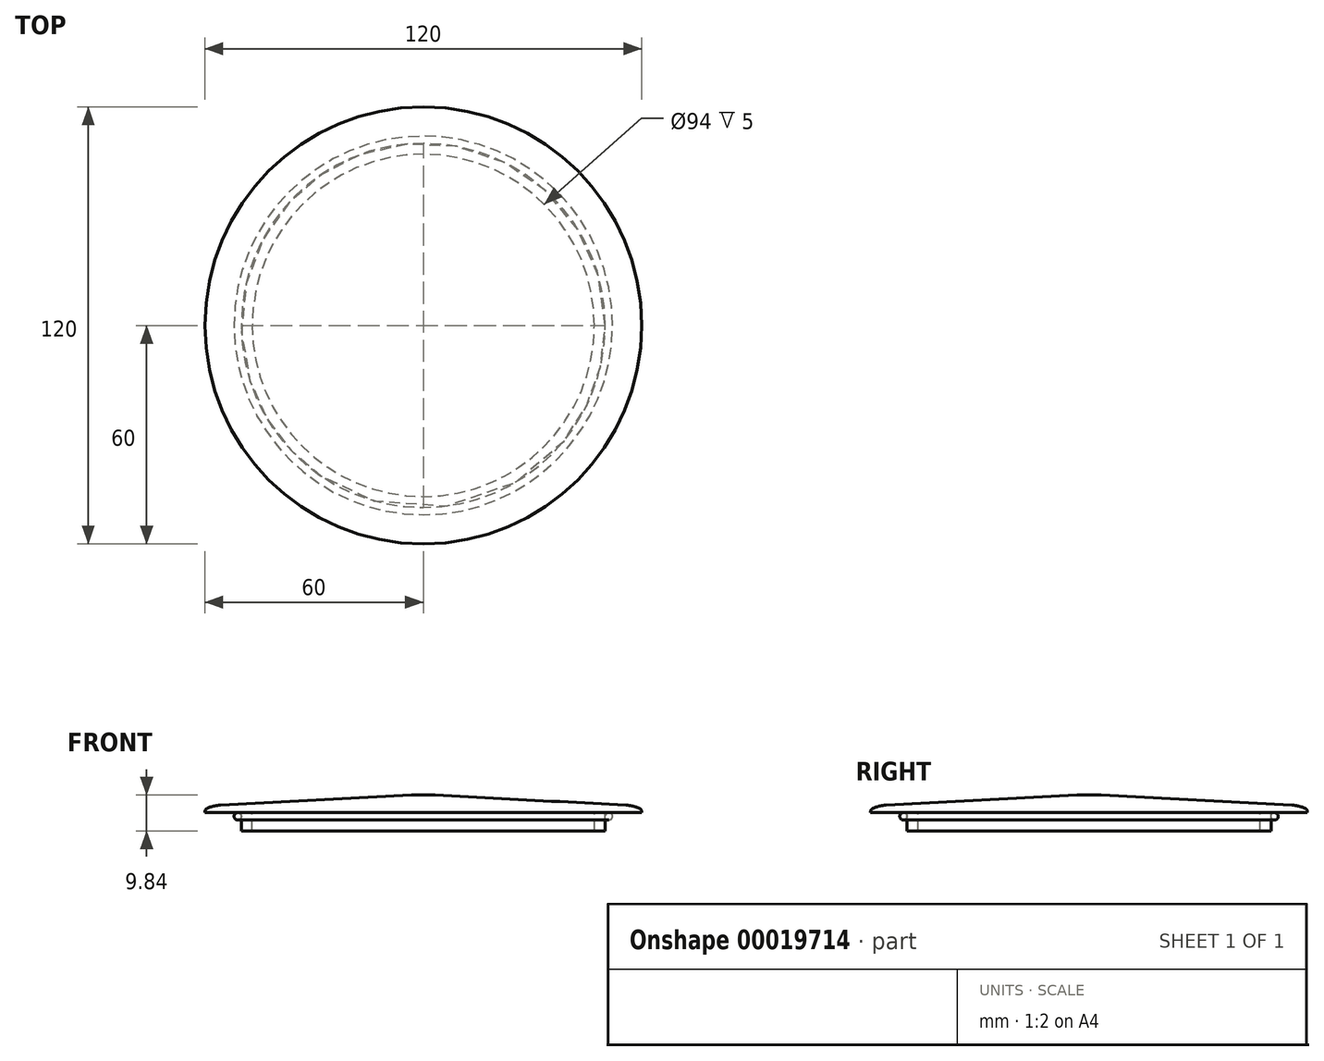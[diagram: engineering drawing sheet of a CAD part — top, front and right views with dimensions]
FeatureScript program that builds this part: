
annotation { "Feature Type Name" : "Feature", "Feature Type Description" : "" }
export const myFeature = defineFeature(function(context is Context, id is Id, definition is map)
    precondition{}
    {
        {
            var Q0;
            Q0=qCreatedBy(makeId("Front.planeOp"),FACE);
            var sketch = newSketch(context, id + "F0", { "sketchPlane" : qUnion([Q0])});
            skLineSegment(sketch, "E0", {"start": v(50, 0) * mm, "end": v(50, 5) * mm});
            skLineSegment(sketch, "E1", {"start": v(50, 5) * mm, "end": v(60, 5) * mm});
            skLineSegment(sketch, "E2", {"start": v(59.33, 6.24) * mm, "end": v(58.56, 6.51) * mm});
            skLineSegment(sketch, "E3", {"start": v(0, 9.84) * mm, "end": v(2.74, 9.84) * mm});
            skLineSegment(sketch, "E4", {"start": v(3.26, 9.83) * mm, "end": v(55.73, 7.08) * mm});
            skPoint(sketch, "E5.visualSharp", {"position": v(57.19, 7) * mm});
            skArc(sketch, "E5.filletArc", {"start": v(58.56, 6.51) * mm, "mid": v(57.17, 6.9) * mm, "end": v(55.73, 7.08) * mm});
            skPoint(sketch, "E6.visualSharp", {"position": v(3, 9.84) * mm});
            skArc(sketch, "E6.filletArc", {"start": v(3.26, 9.83) * mm, "mid": v(3, 9.84) * mm, "end": v(2.74, 9.84) * mm});
            skLineSegment(sketch, "E7", {"start": v(0, 27.32) * mm, "end": v(0, -17.32) * mm, "construction": true});
            skLineSegment(sketch, "E8", {"start": v(60, 5) * mm, "end": v(60, 5.3) * mm});
            skPoint(sketch, "E9.visualSharp", {"position": v(60, 6) * mm});
            skArc(sketch, "E9.filletArc", {"start": v(60, 5.3) * mm, "mid": v(59.82, 5.87) * mm, "end": v(59.33, 6.24) * mm});
            skLineSegment(sketch, "E10", {"start": v(42.44, 0) * mm, "end": v(42.47, 0) * mm});
            skLineSegment(sketch, "E11", {"start": v(47, 0) * mm, "end": v(50, 0) * mm});
            skLineSegment(sketch, "E12", {"start": v(44.72, 0) * mm, "end": v(47, 0) * mm});
            skLineSegment(sketch, "E13", {"start": v(47, 0) * mm, "end": v(47, 5) * mm});
            skLineSegment(sketch, "E14", {"start": v(47, 5) * mm, "end": v(0, 5) * mm});
            skLineSegment(sketch, "E15", {"start": v(0, 9.84) * mm, "end": v(0, 5) * mm});
            skSolve(sketch);
        }
        {
            var Q0;
            Q0 = qSketchRegion(id + "F0", true);
            var Q1;
            Q1=sQuery(id+"F0.wireOp",EDGE,"E7");
            revolve(context, id + "F1", {"entities" : qUnion([Q0]), "axis" : qUnion([Q1]), "revolveType" : RevolveType.FULL});
        }
        {
            var Q0;
            Q0=qCreatedBy(makeId("Front.planeOp"),FACE);
            var sketch = newSketch(context, id + "F2", { "sketchPlane" : qUnion([Q0])});
            skCircle(sketch, "E16", {"center": v(51, 4) * mm, "radius": 1 * mm});
            skSolve(sketch);
        }
        {
            var Q0;
            Q0 = qSketchRegion(id + "F2", true);
            var Q1;
            Q1=sQuery(id+"F0.wireOp",EDGE,"E7");
            revolve(context, id + "F3", {"entities" : qUnion([Q0]), "axis" : qUnion([Q1]), "revolveType" : RevolveType.FULL});
        }
    });
